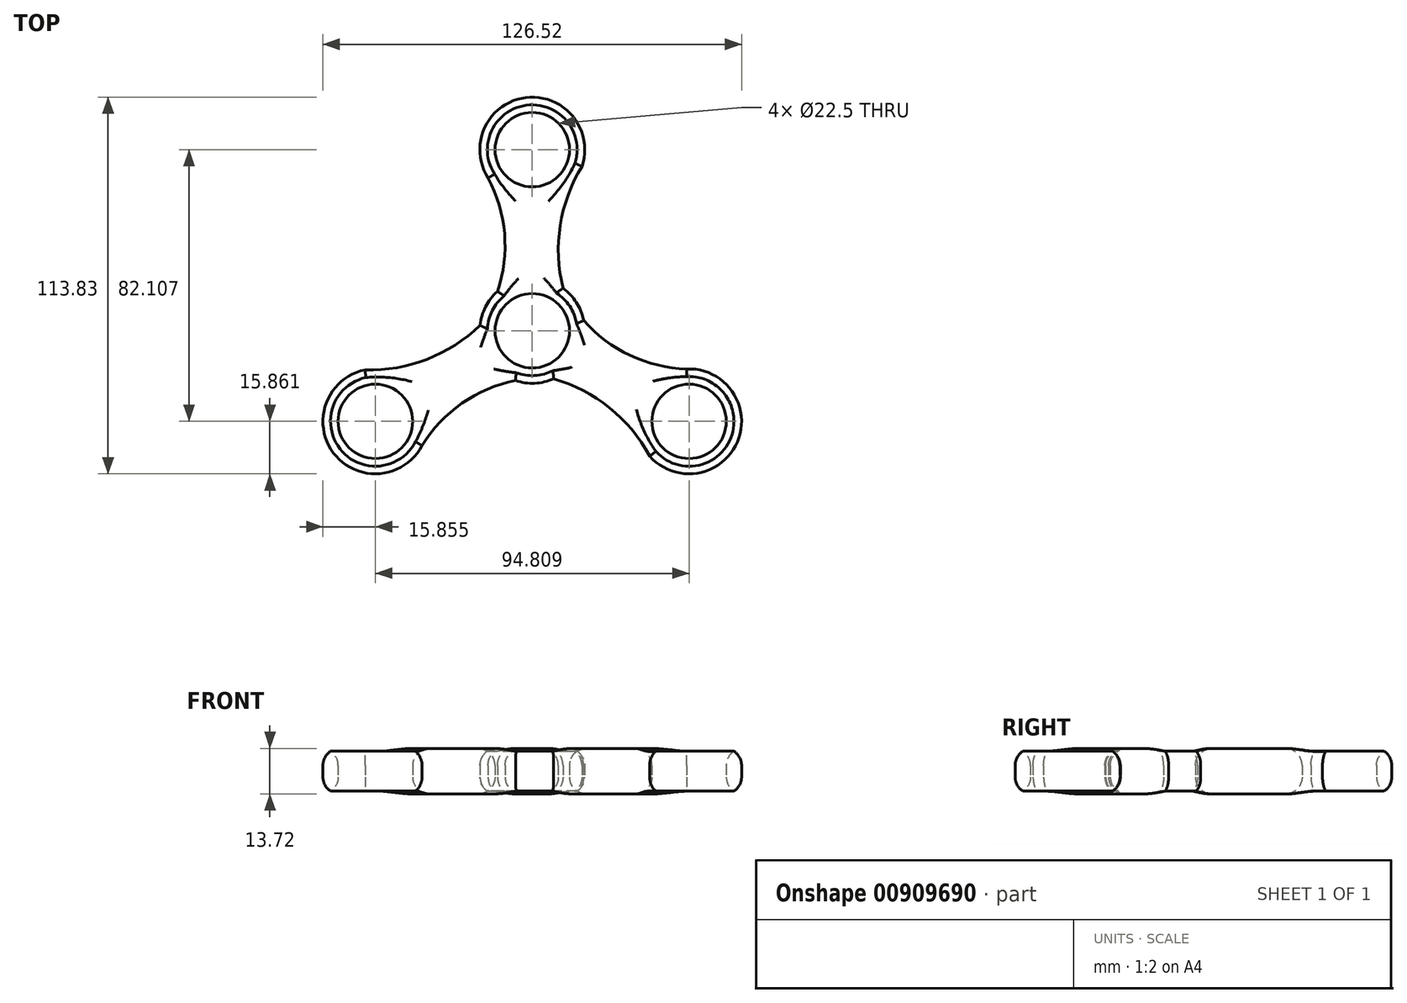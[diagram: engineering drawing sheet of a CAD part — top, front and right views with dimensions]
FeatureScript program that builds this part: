
annotation { "Feature Type Name" : "Feature", "Feature Type Description" : "" }
export const myFeature = defineFeature(function(context is Context, id is Id, definition is map)
    precondition{}
    {
        {
            var Q0;
            Q0=qCreatedBy(makeId("Top.planeOp"),FACE);
            var sketch = newSketch(context, id + "F0", { "sketchPlane" : qUnion([Q0])});
            skCircle(sketch, "E0", {"center": v(0, 0) * mm, "radius": 11.25 * mm});
            skArc(sketch, "E1", {"start": v(-10.5, 11.89) * mm, "mid": v(-14.1, 7.26) * mm, "end": v(-15.77, 1.64) * mm});
            skCircle(sketch, "E2", {"center": v(0, 54.74) * mm, "radius": 11.25 * mm});
            skCircle(sketch, "E3", {"center": v(0, 54.74) * mm, "radius": 15.86 * mm});
            skCircle(sketch, "E4.1.0", {"center": v(-47.4, -27.37) * mm, "radius": 11.25 * mm});
            skCircle(sketch, "E4.1.1", {"center": v(-47.4, -27.37) * mm, "radius": 15.86 * mm});
            skCircle(sketch, "E4.2.0", {"center": v(47.4, -27.37) * mm, "radius": 11.25 * mm});
            skCircle(sketch, "E4.2.1", {"center": v(47.4, -27.37) * mm, "radius": 15.86 * mm});
            skArc(sketch, "E5", {"start": v(-10.5, 11.89) * mm, "mid": v(-8.37, 29.33) * mm, "end": v(-13.35, 46.18) * mm});
            skArc(sketch, "E6", {"start": v(15.02, 49.66) * mm, "mid": v(8.45, 31.83) * mm, "end": v(9.3, 12.84) * mm});
            skArc(sketch, "E7.1.0", {"start": v(-5.05, -15.03) * mm, "mid": v(-21.22, -21.91) * mm, "end": v(-33.32, -34.65) * mm});
            skArc(sketch, "E7.1.1", {"start": v(-50.51, -11.82) * mm, "mid": v(-31.79, -8.6) * mm, "end": v(-15.77, 1.64) * mm});
            skArc(sketch, "E7.2.0", {"start": v(15.54, 3.15) * mm, "mid": v(29.58, -7.42) * mm, "end": v(46.66, -11.53) * mm});
            skArc(sketch, "E7.2.1", {"start": v(35.5, -37.84) * mm, "mid": v(23.34, -23.23) * mm, "end": v(6.47, -14.48) * mm});
            skArc(sketch, "E8.trimOffspring", {"start": v(-5.05, -15.03) * mm, "mid": v(0.76, -15.84) * mm, "end": v(6.47, -14.48) * mm});
            skArc(sketch, "E9.trimOffspring", {"start": v(15.54, 3.15) * mm, "mid": v(13.34, 8.58) * mm, "end": v(9.3, 12.84) * mm});
            skCircle(sketch, "E10", {"center": v(-91.55, -6.8) * mm, "radius": 26.93 * mm});
            skSolve(sketch);
        }
        {
            var Q0;
            Q0=makeQuery(id+"F0.imprint","IMPRINT",FACE,{"disambiguationData":[TD([[makeQuery(id+"F0.imprint","IMPRINT",EDGE,{"derivedFrom":sQuery(id+"F0.wireOp",EDGE,"E0")}),-1.0]])]});
            var Q1;
            Q1=makeQuery(id+"F0.imprint","IMPRINT",FACE,{"disambiguationData":[TD([[makeQuery(id+"F0.imprint","IMPRINT",EDGE,{"derivedFrom":sQuery(id+"F0.wireOp",EDGE,"E2")}),-1.0]])]});
            var Q2;
            Q2=makeQuery(id+"F0.imprint","IMPRINT",FACE,{"disambiguationData":[TD([[makeQuery(id+"F0.imprint","IMPRINT",EDGE,{"derivedFrom":sQuery(id+"F0.wireOp",EDGE,"E4.2.0")}),-1.0]])]});
            var Q3;
            Q3=makeQuery(id+"F0.imprint","IMPRINT",FACE,{"disambiguationData":[TD([[makeQuery(id+"F0.imprint","IMPRINT",EDGE,{"derivedFrom":sQuery(id+"F0.wireOp",EDGE,"E4.1.0")}),-1.0]])]});
            extrude(context, id + "F1", {"entities" : qUnion([Q0, Q1, Q2, Q3]), "depth" : 13.72 * mm, "offsetDistance" : 25.4 * mm});
        }
        {
            var Q0;
            Q0=makeQuery(id+"F1.opExtrude","CAP_FACE",FACE,{"disambiguationData":[OSD([sQuery(id+"F0.wireOp",EDGE,"E0"),sQuery(id+"F0.wireOp",EDGE,"E1"),sQuery(id+"F0.wireOp",EDGE,"E2"),sQuery(id+"F0.wireOp",EDGE,"E3"),sQuery(id+"F0.wireOp",EDGE,"E4.1.0"),sQuery(id+"F0.wireOp",EDGE,"E4.1.1"),sQuery(id+"F0.wireOp",EDGE,"E4.2.0"),sQuery(id+"F0.wireOp",EDGE,"E4.2.1"),sQuery(id+"F0.wireOp",EDGE,"E5"),sQuery(id+"F0.wireOp",EDGE,"E6"),sQuery(id+"F0.wireOp",EDGE,"E7.1.0"),sQuery(id+"F0.wireOp",EDGE,"E7.1.1"),sQuery(id+"F0.wireOp",EDGE,"E7.2.0"),sQuery(id+"F0.wireOp",EDGE,"E7.2.1"),sQuery(id+"F0.wireOp",EDGE,"E8.trimOffspring"),sQuery(id+"F0.wireOp",EDGE,"E9.trimOffspring")])],"isStart":false});
            fillet(context, id + "F2", {"entities" : qUnion([Q0]), "radius" : 5.08 * mm, "tangentPropagation" : true, "allowEdgeOverflow" : false});
        }
        {
            var Q0;
            Q0=makeQuery(id+"F1.opExtrude","CAP_FACE",FACE,{"disambiguationData":[OSD([sQuery(id+"F0.wireOp",EDGE,"E0"),sQuery(id+"F0.wireOp",EDGE,"E1"),sQuery(id+"F0.wireOp",EDGE,"E2"),sQuery(id+"F0.wireOp",EDGE,"E3"),sQuery(id+"F0.wireOp",EDGE,"E4.1.0"),sQuery(id+"F0.wireOp",EDGE,"E4.1.1"),sQuery(id+"F0.wireOp",EDGE,"E4.2.0"),sQuery(id+"F0.wireOp",EDGE,"E4.2.1"),sQuery(id+"F0.wireOp",EDGE,"E5"),sQuery(id+"F0.wireOp",EDGE,"E6"),sQuery(id+"F0.wireOp",EDGE,"E7.1.0"),sQuery(id+"F0.wireOp",EDGE,"E7.1.1"),sQuery(id+"F0.wireOp",EDGE,"E7.2.0"),sQuery(id+"F0.wireOp",EDGE,"E7.2.1"),sQuery(id+"F0.wireOp",EDGE,"E8.trimOffspring"),sQuery(id+"F0.wireOp",EDGE,"E9.trimOffspring")])],"isStart":true});
            fillet(context, id + "F3", {"entities" : qUnion([Q0]), "radius" : 5.08 * mm, "tangentPropagation" : true, "allowEdgeOverflow" : false});
        }
    });
